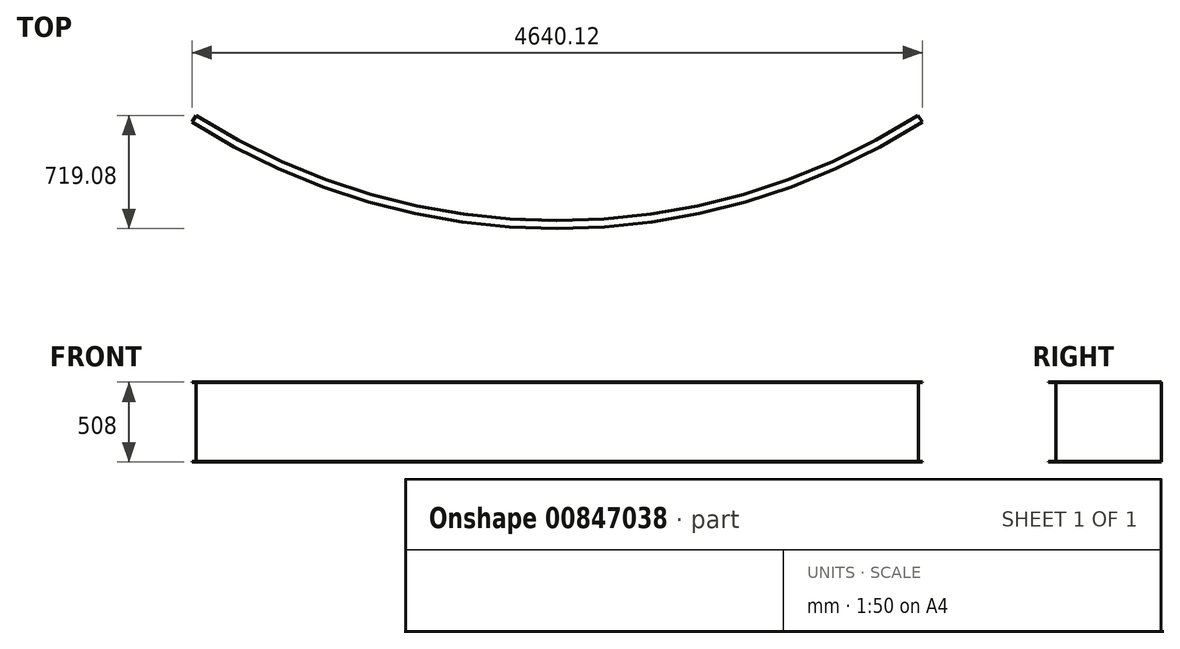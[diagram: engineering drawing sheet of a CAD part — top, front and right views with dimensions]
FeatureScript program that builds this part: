
annotation { "Feature Type Name" : "Feature", "Feature Type Description" : "" }
export const myFeature = defineFeature(function(context is Context, id is Id, definition is map)
    precondition{}
    {
        {
            var Q0;
            Q0=qCreatedBy(makeId("Right.planeOp"),FACE);
            var sketch = newSketch(context, id + "F0", { "sketchPlane" : qUnion([Q0])});
            skLineSegment(sketch, "E0", {"start": v(0, 0) * mm, "end": v(0, 508) * mm});
            skLineSegment(sketch, "E1", {"start": v(0, 508) * mm, "end": v(-50.8, 508) * mm});
            skLineSegment(sketch, "E2", {"start": v(-50.8, 508) * mm, "end": v(-50.8, 504.82) * mm});
            skLineSegment(sketch, "E3", {"start": v(-50.8, 504.82) * mm, "end": v(-3.18, 504.82) * mm});
            skLineSegment(sketch, "E4", {"start": v(-3.18, 504.82) * mm, "end": v(-3.17, 3.18) * mm});
            skLineSegment(sketch, "E5", {"start": v(-3.17, 3.18) * mm, "end": v(-50.8, 3.18) * mm});
            skLineSegment(sketch, "E6", {"start": v(-50.8, 3.17) * mm, "end": v(-50.8, 0) * mm});
            skLineSegment(sketch, "E7", {"start": v(-50.8, 0) * mm, "end": v(0, 0) * mm});
            skSolve(sketch);
        }
        {
            var Q0;
            Q0=qCreatedBy(makeId("Right.planeOp"),FACE);
            var sketch = newSketch(context, id + "F1", { "sketchPlane" : qUnion([Q0])});
            skLineSegment(sketch, "E8", {"start": v(4267.2, 0) * mm, "end": v(4267.2, 11323.5) * mm, "construction": true});
            skSolve(sketch);
        }
        {
            var Q0;
            Q0=makeQuery(id+"F0.imprint","IMPRINT",FACE,{"disambiguationData":[TD([[makeQuery(id+"F0.imprint","IMPRINT",EDGE,{"derivedFrom":sQuery(id+"F0.wireOp",EDGE,"E0")}),1.0]])]});
            var Q1;
            Q1=sQuery(id+"F1.wireOp",EDGE,"E8");
            revolve(context, id + "F2", {"surfaceOperationType" : NewSurfaceOperationType.NEW, "entities" : qUnion([Q0]), "axis" : qUnion([Q1]), "revolveType" : RevolveType.SYMMETRIC, "angle" : 65 * degree});
        }
    });
